# Revit family: Towel Rail-Single-Caroma Cosmo Metal
name_source: partatom
category: Specialty Equipment
revit_build: Autodesk Revit 2013 (Build: 20121003_2115(x64)
units: mm (PartAtom-declared; Revit-internal decimal feet)

## types (3) — shared parameters
Assembly Code = C1030200
Default Elevation = 900 mm  [stored 2.95276 ft]
Manufacturer = GWA Bathrooms & Kitchens
Material_ANZRS = Metal-Chrome-Caroma
ModifiedIssue_ANZRS = 1 $
URL = http://www.caroma.com.au
zero-valued in all types: Cost

## per-type parameters (varying)
| type | Length_ANZRS | Model | Size | Type Comments |
| Hand Towel Rail-200mm | 190 mm  [stored 0.62336 ft] | 308128C | 1 | Caroma Cosmo Metal Hand Towel Rail 200mm |
| Single Towel Rail-600mm | 590 mm  [stored 1.9357 ft] | 306128C | 2 | Caroma Cosmo Metal Single Towel Rail 600mm |
| Single Towel Rail-900mm | 890 mm  [stored 2.91995 ft] | 306132C | 3 | Caroma Cosmo Metal Single Towel Rail 900mm |

note: [stored X ft] marks values corroborated as IEEE doubles in the binary element streams (Revit-internal decimal feet)

## geometry (parser evidence)
native form markers: Blend x8, Sweep x1
no freeform markers — native parametric forms only
